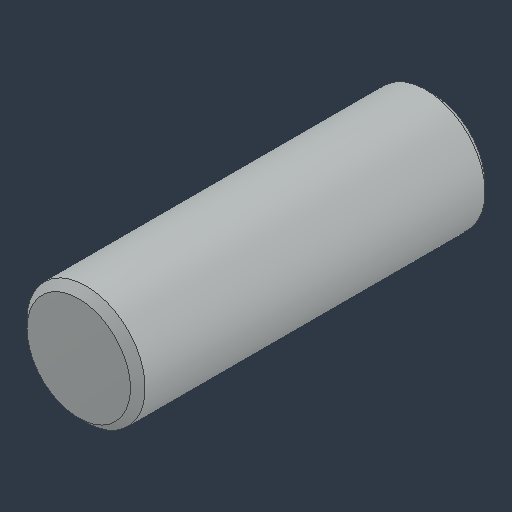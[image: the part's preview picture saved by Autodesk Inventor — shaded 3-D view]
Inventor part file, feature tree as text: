
AUTODESK INVENTOR PART (.ipt)
format: ipt  version: 2024.3 (Build 283343000, 343)  size: 98,304 bytes
history: native  units: in
note: dims shown in document units (in); Inventor stores cm internally (conversion verified against a paired STEP export)
features: chamfer x1
ambient origin geometry x8: Origin, YZ Plane, XZ Plane, XY Plane, X Axis, Y Axis, Z Axis, Center Point
bodies: Solid1 (feature_tree)
feature tree (1):
  chamfer  "Chamfer1"  [1 undecoded]
note: 1 required parameter value undecoded (feature->parameter linkage not recoverable at this tier; creation-order binding heuristic only, values carry confidence <= 0.55)
